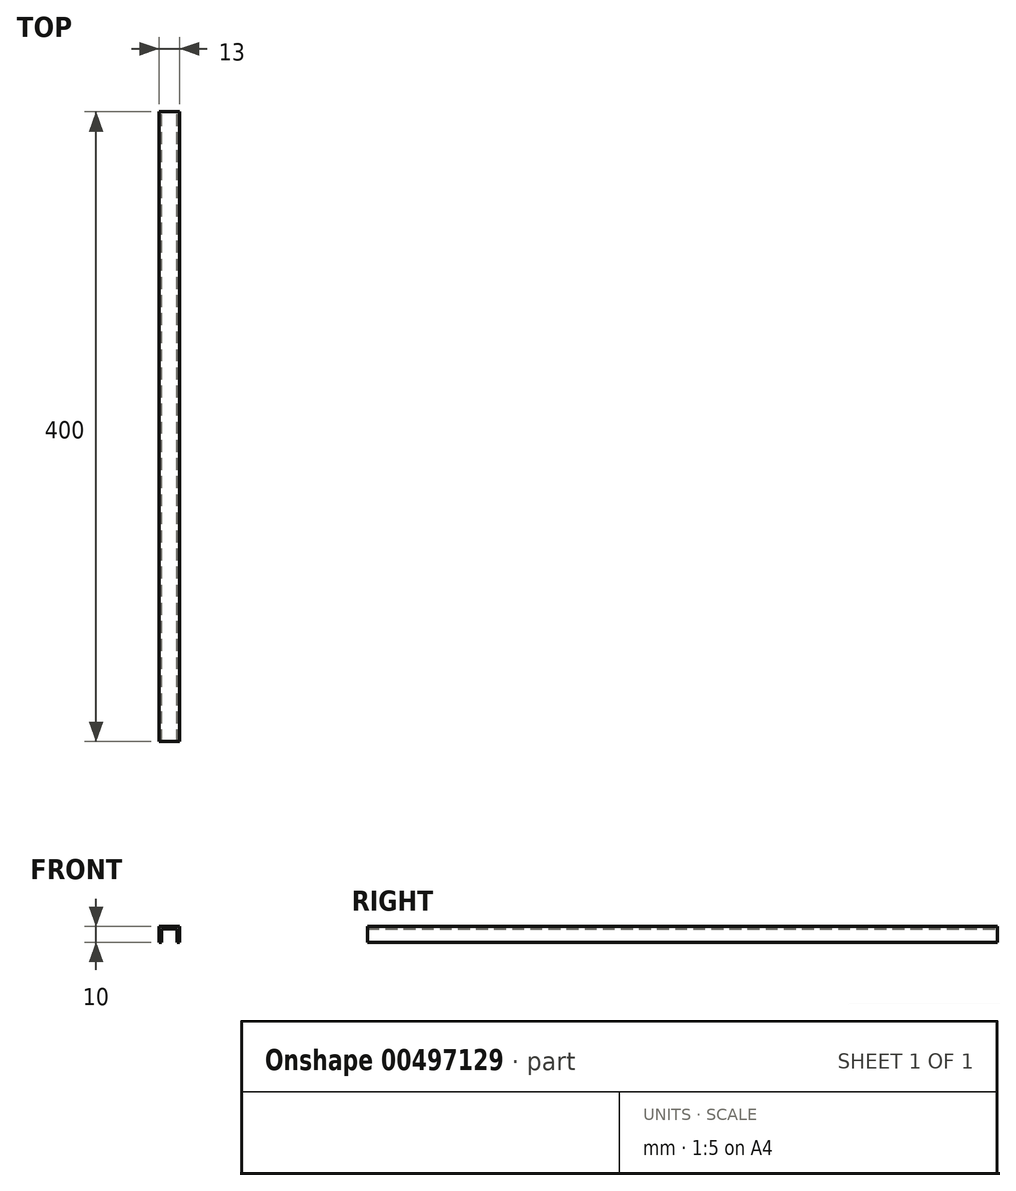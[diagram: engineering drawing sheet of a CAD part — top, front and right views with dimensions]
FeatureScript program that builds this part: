
annotation { "Feature Type Name" : "Feature", "Feature Type Description" : "" }
export const myFeature = defineFeature(function(context is Context, id is Id, definition is map)
    precondition{}
    {
        {
            var Q0;
            Q0=qCreatedBy(makeId("Front.planeOp"),FACE);
            var sketch = newSketch(context, id + "F0", { "sketchPlane" : qUnion([Q0])});
            skLineSegment(sketch, "E0.bottom", {"start": v(3.26, 0.03) * mm, "end": v(16.26, 0.03) * mm});
            skLineSegment(sketch, "E0.left", {"start": v(3.26, 0.03) * mm, "end": v(3.26, -9.97) * mm});
            skLineSegment(sketch, "E0.right", {"start": v(16.26, 0.03) * mm, "end": v(16.26, -9.97) * mm});
            skLineSegment(sketch, "E1.0", {"start": v(4.76, -1.47) * mm, "end": v(4.76, -9.97) * mm});
            skLineSegment(sketch, "E1.1", {"start": v(4.76, -1.47) * mm, "end": v(14.76, -1.47) * mm});
            skLineSegment(sketch, "E1.2", {"start": v(14.76, -1.47) * mm, "end": v(14.76, -9.97) * mm});
            skLineSegment(sketch, "E2", {"start": v(3.26, -9.97) * mm, "end": v(4.76, -9.97) * mm});
            skLineSegment(sketch, "E3", {"start": v(14.76, -9.97) * mm, "end": v(16.26, -9.97) * mm});
            skSolve(sketch);
        }
        {
            var Q0;
            Q0=makeQuery(id+"F0.imprint","IMPRINT",FACE,{"disambiguationData":[TD([[makeQuery(id+"F0.imprint","IMPRINT",EDGE,{"derivedFrom":sQuery(id+"F0.wireOp",EDGE,"E0.bottom")}),-1.0]])]});
            extrude(context, id + "F1", {"entities" : qUnion([Q0]), "depth" : 400 * mm});
        }
    });
